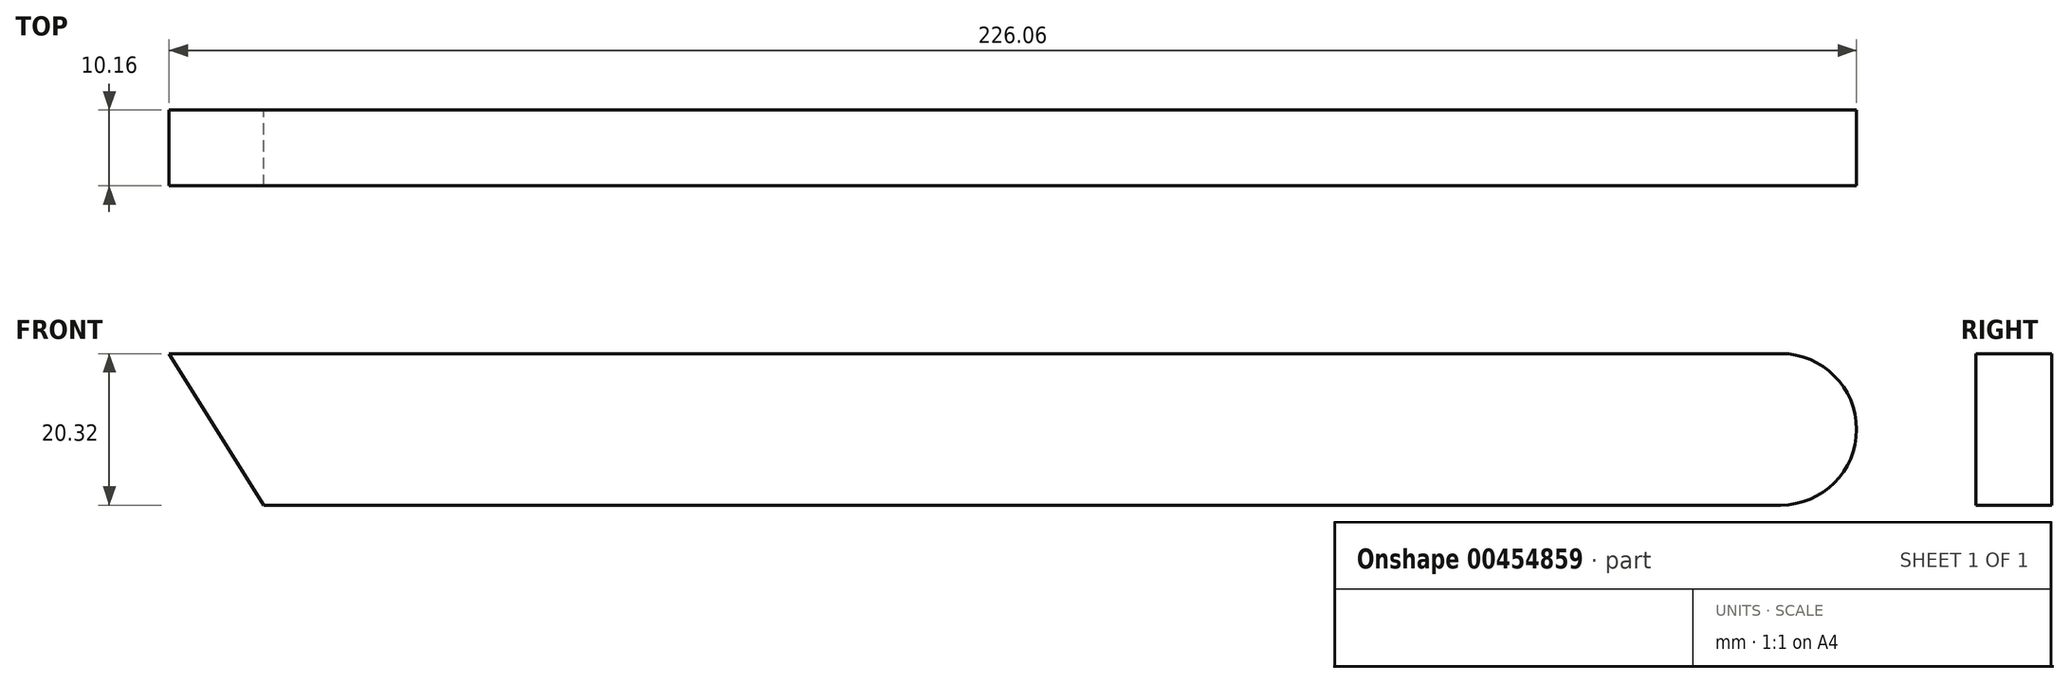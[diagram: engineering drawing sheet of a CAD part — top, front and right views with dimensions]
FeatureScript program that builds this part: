
annotation { "Feature Type Name" : "Feature", "Feature Type Description" : "" }
export const myFeature = defineFeature(function(context is Context, id is Id, definition is map)
    precondition{}
    {
        {
            var Q0;
            Q0=qCreatedBy(makeId("Front.planeOp"),FACE);
            var sketch = newSketch(context, id + "F0", { "sketchPlane" : qUnion([Q0])});
            skCircle(sketch, "E0", {"center": v(0, 0) * mm, "radius": 10.16 * mm});
            skLineSegment(sketch, "E1.bottom", {"start": v(0, 10.16) * mm, "end": v(-203.2, 10.16) * mm});
            skLineSegment(sketch, "E1.top", {"start": v(0, -10.16) * mm, "end": v(-203.2, -10.16) * mm});
            skLineSegment(sketch, "E1.left", {"start": v(0, 10.16) * mm, "end": v(0, -10.16) * mm});
            skLineSegment(sketch, "E1.right", {"start": v(-203.2, 10.16) * mm, "end": v(-203.2, -10.16) * mm});
            skLineSegment(sketch, "E2", {"start": v(-203.2, -10.16) * mm, "end": v(-215.9, 10.16) * mm});
            skLineSegment(sketch, "E3", {"start": v(-215.9, 10.16) * mm, "end": v(-203.2, 10.16) * mm});
            skSolve(sketch);
        }
        {
            var Q0;
            Q0=makeQuery(id+"F0.imprint","IMPRINT",FACE,{"disambiguationData":[TD([[makeQuery(id+"F0.imprint","IMPRINT",EDGE,{"derivedFrom":sQuery(id+"F0.wireOp",EDGE,"E0")}),1.0]])]});
            extrude(context, id + "F1", {"entities" : qUnion([Q0]), "endBound" : BoundingType.SYMMETRIC, "depth" : 10.16 * mm, "offsetDistance" : 25.4 * mm});
        }
        {
            var Q0;
            {var subQ1=sQuery(id+"F0.wireOp",EDGE,"E1.bottom");Q0=makeQuery(id+"F0.imprint","IMPRINT",FACE,{"disambiguationData":[TD([[makeQuery(id+"F0.imprint","IMPRINT",EDGE,{"derivedFrom":subQ1}),1.0]])]});}
            var Q1;
            Q1=makeQuery(id+"F0.imprint","IMPRINT",FACE,{"disambiguationData":[TD([[makeQuery(id+"F0.imprint","IMPRINT",EDGE,{"derivedFrom":sQuery(id+"F0.wireOp",EDGE,"E1.right")}),-1.0]])]});
            extrude(context, id + "F2", {"entities" : qUnion([Q0, Q1]), "operationType" : NewBodyOperationType.ADD, "endBound" : BoundingType.SYMMETRIC, "depth" : 10.16 * mm, "offsetDistance" : 25.4 * mm});
        }
    });
